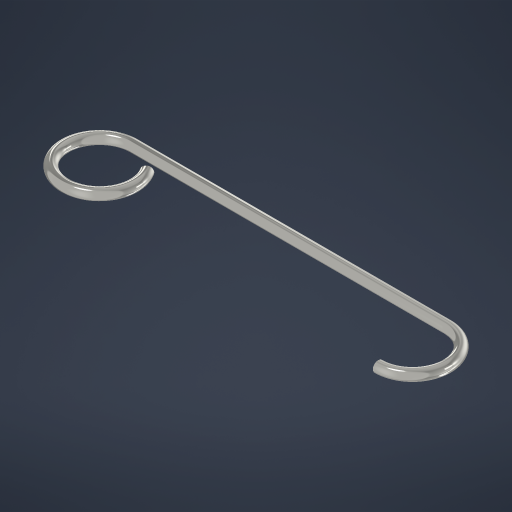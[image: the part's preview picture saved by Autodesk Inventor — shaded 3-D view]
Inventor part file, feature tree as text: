
AUTODESK INVENTOR PART (.ipt)
format: ipt  version: 2024 (Build 280153000, 153)  size: 275,456 bytes
history: native  units: mm
features: other x5, sweep x1, plane x1, sketch x1
ambient origin geometry x8: Origin, YZ Plane, XZ Plane, XY Plane, X Axis, Y Axis, Z Axis, Center Point
bodies: Body1 (feature_tree)
feature tree (8):
  other  "Sólido1"
  sweep  "Barrido1"
  plane  "Plano de trabajo3"
  sketch  "Boceto5"  dims[d3=2.0mm d4=4.0mm d5=0.0mm d6=0.0mm d7=118.313mm d8=148.313mm d9=118.313mm d10=118.313mm]
  other  "Punto de trabajo8"
  other  "Punto de trabajo9"
  other  "Punto de trabajo12"
  other  "Punto de trabajo13"
